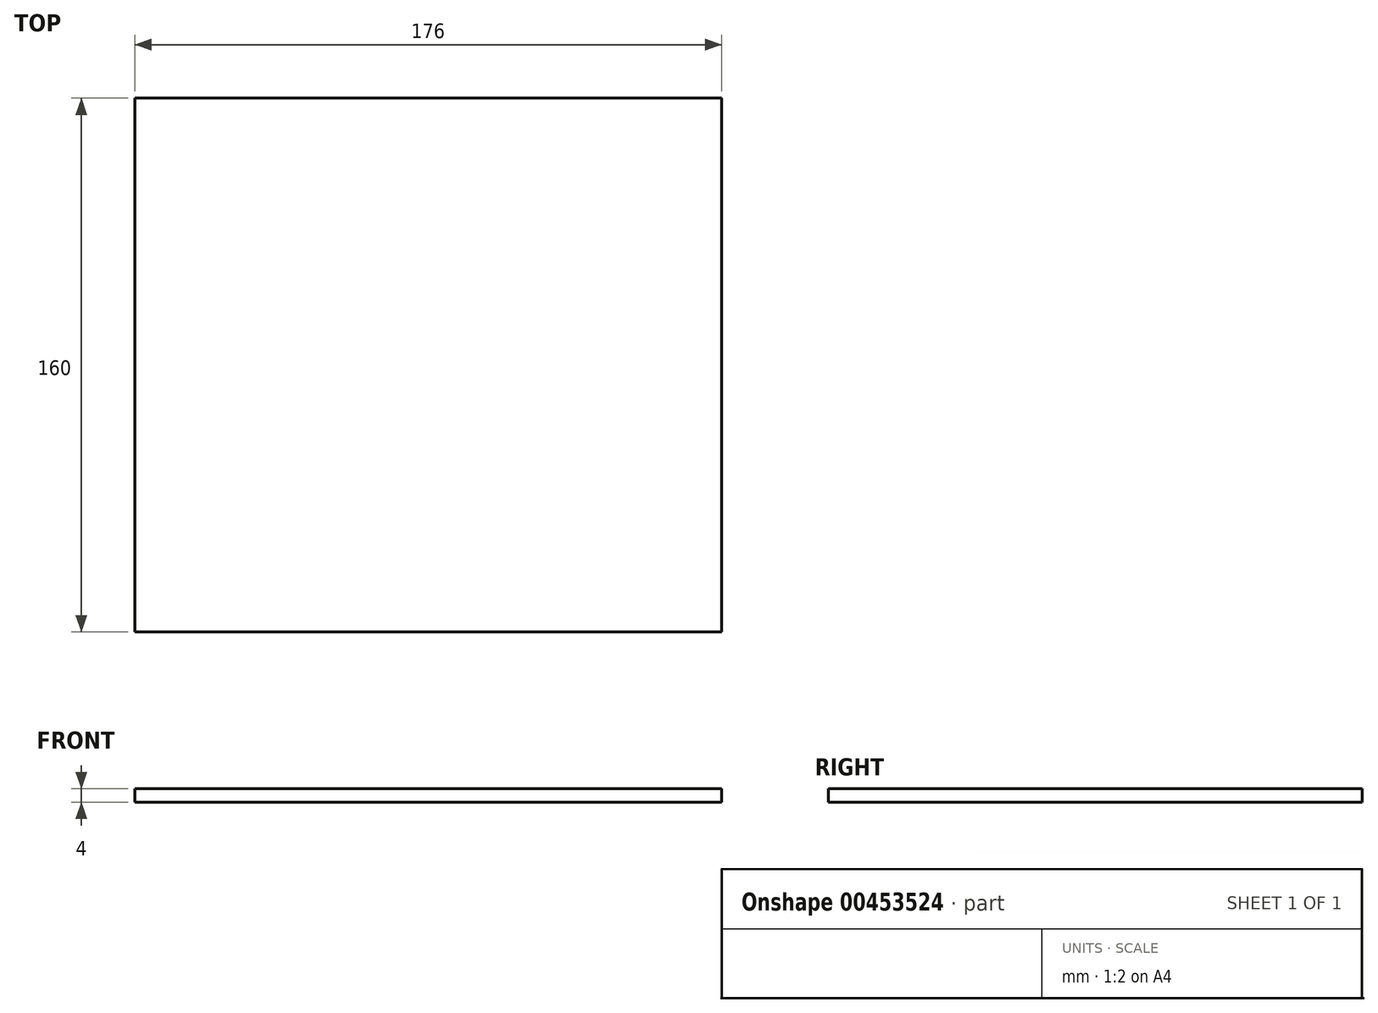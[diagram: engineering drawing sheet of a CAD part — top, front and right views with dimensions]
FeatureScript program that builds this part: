
annotation { "Feature Type Name" : "Feature", "Feature Type Description" : "" }
export const myFeature = defineFeature(function(context is Context, id is Id, definition is map)
    precondition{}
    {
        {
            var Q0;
            Q0=qCreatedBy(makeId("Top.planeOp"),FACE);
            var sketch = newSketch(context, id + "F0", { "sketchPlane" : qUnion([Q0])});
            skLineSegment(sketch, "E0.bottom", {"start": v(88, -80) * mm, "end": v(-88, -80) * mm});
            skLineSegment(sketch, "E0.top", {"start": v(88, 80) * mm, "end": v(-88, 80) * mm});
            skLineSegment(sketch, "E0.left", {"start": v(88, -80) * mm, "end": v(88, 80) * mm});
            skLineSegment(sketch, "E0.right", {"start": v(-88, -80) * mm, "end": v(-88, 80) * mm});
            skPoint(sketch, "E0.middle", {"position": v(0, 0) * mm});
            skSolve(sketch);
        }
        {
            var Q0;
            Q0=makeQuery(id+"F0.imprint","IMPRINT",FACE,{"disambiguationData":[TD([[makeQuery(id+"F0.imprint","IMPRINT",EDGE,{"derivedFrom":sQuery(id+"F0.wireOp",EDGE,"E0.bottom")}),-1.0]])]});
            extrude(context, id + "F1", {"entities" : qUnion([Q0]), "depth" : 4 * mm});
        }
    });
